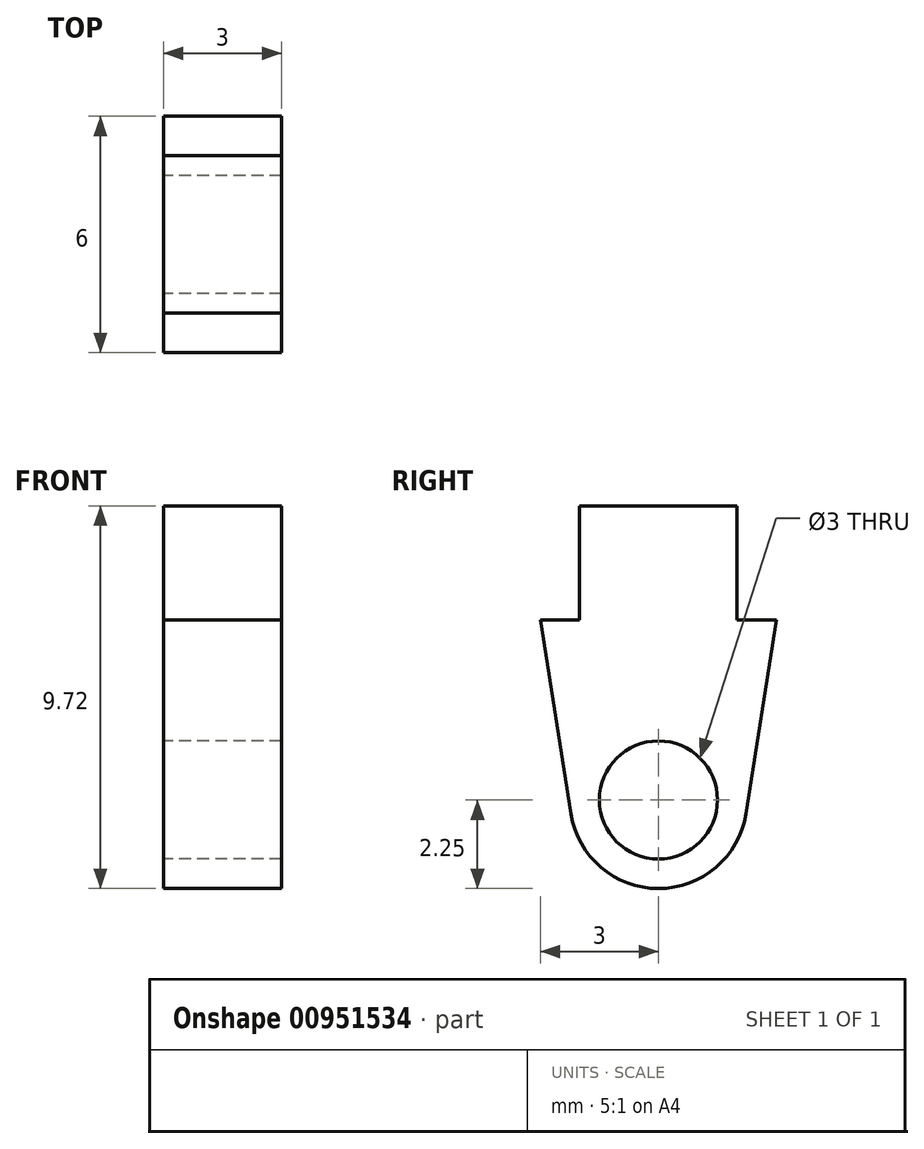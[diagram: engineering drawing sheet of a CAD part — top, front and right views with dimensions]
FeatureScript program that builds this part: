
annotation { "Feature Type Name" : "Feature", "Feature Type Description" : "" }
export const myFeature = defineFeature(function(context is Context, id is Id, definition is map)
    precondition{}
    {
        {
            var Q0;
            Q0=qCreatedBy(makeId("Right.planeOp"),FACE);
            var sketch = newSketch(context, id + "F0", { "sketchPlane" : qUnion([Q0])});
            skCircle(sketch, "E0", {"center": v(0, 0) * mm, "radius": 1.5 * mm});
            skCircle(sketch, "E1", {"center": v(0, 0) * mm, "radius": 2.25 * mm});
            skLineSegment(sketch, "E2.bottom", {"start": v(2, 4.57) * mm, "end": v(-2, 4.57) * mm});
            skLineSegment(sketch, "E2.top", {"start": v(2, 7.47) * mm, "end": v(-2, 7.47) * mm});
            skLineSegment(sketch, "E2.left", {"start": v(2, 4.57) * mm, "end": v(2, 7.47) * mm});
            skLineSegment(sketch, "E2.right", {"start": v(-2, 4.57) * mm, "end": v(-2, 7.47) * mm});
            skPoint(sketch, "E2.middle", {"position": v(0, 6.02) * mm});
            skLineSegment(sketch, "E3", {"start": v(-2, 4.57) * mm, "end": v(-3, 4.57) * mm});
            skLineSegment(sketch, "E4", {"start": v(2, 4.57) * mm, "end": v(3, 4.57) * mm});
            skLineSegment(sketch, "E5", {"start": v(3, 4.57) * mm, "end": v(2.22, -0.35) * mm});
            skLineSegment(sketch, "E6", {"start": v(-3, 4.57) * mm, "end": v(-2.22, -0.35) * mm});
            skSolve(sketch);
        }
        {
            var Q0;
            Q0 = qSketchRegion(id + "F0", true);
            extrude(context, id + "F1", {"entities" : qUnion([Q0]), "depth" : 3 * mm, "offsetDistance" : 25 * mm});
        }
    });
